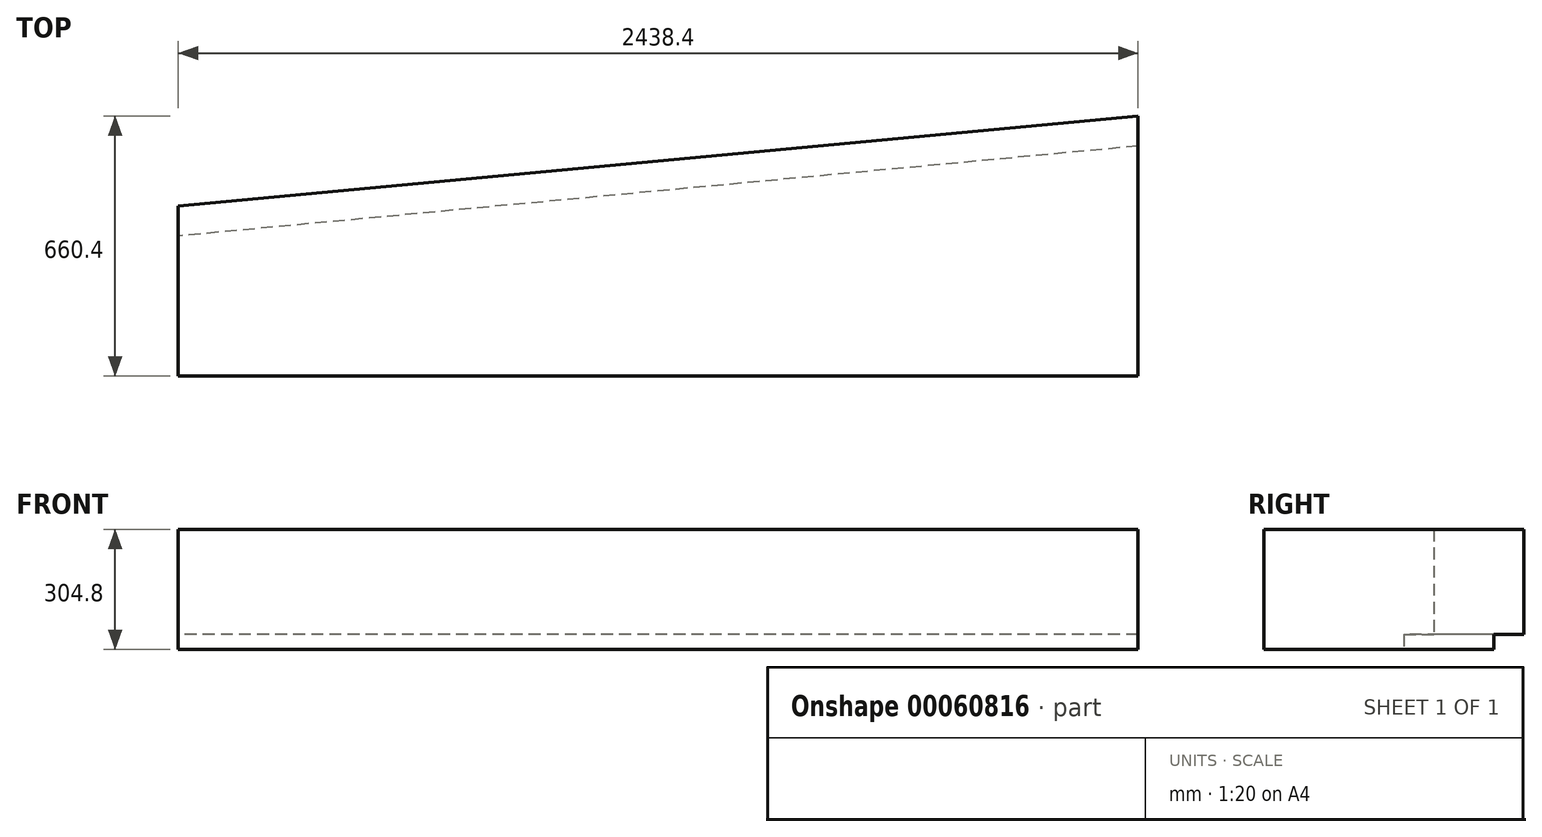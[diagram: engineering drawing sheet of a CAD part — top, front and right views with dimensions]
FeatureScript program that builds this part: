
annotation { "Feature Type Name" : "Feature", "Feature Type Description" : "" }
export const myFeature = defineFeature(function(context is Context, id is Id, definition is map)
    precondition{}
    {
        {
            var Q0;
            Q0=qCreatedBy(makeId("Top.planeOp"),FACE);
            var sketch = newSketch(context, id + "F0", { "sketchPlane" : qUnion([Q0])});
            skLineSegment(sketch, "E0", {"start": v(0, 0) * mm, "end": v(0, 431.8) * mm});
            skLineSegment(sketch, "E1", {"start": v(0, 0) * mm, "end": v(2438.4, 0) * mm});
            skLineSegment(sketch, "E2", {"start": v(2438.4, 0) * mm, "end": v(2438.4, 660.4) * mm});
            skLineSegment(sketch, "E3", {"start": v(2438.4, 660.4) * mm, "end": v(0, 431.8) * mm});
            skSolve(sketch);
        }
        {
            var Q0;
            Q0 = qSketchRegion(id + "F0", true);
            extrude(context, id + "F1", {"entities" : qUnion([Q0]), "depth" : 304.8 * mm});
        }
        {
            var Q0;
            Q0=makeQuery(id+"F1.opExtrude","CAP_FACE",FACE,{"disambiguationData":[OSD([sQuery(id+"F0.wireOp",EDGE,"E0"),sQuery(id+"F0.wireOp",EDGE,"E1"),sQuery(id+"F0.wireOp",EDGE,"E2"),sQuery(id+"F0.wireOp",EDGE,"E3")])],"isStart":true});
            var sketch = newSketch(context, id + "F2", { "sketchPlane" : qUnion([Q0])});
            skLineSegment(sketch, "E4", {"start": v(2438.4, -660.4) * mm, "end": v(2438.4, -584.2) * mm});
            skLineSegment(sketch, "E5", {"start": v(0, -431.8) * mm, "end": v(0, -355.6) * mm});
            skLineSegment(sketch, "E6", {"start": v(2438.4, -584.2) * mm, "end": v(0, -355.6) * mm});
            skLineSegment(sketch, "E7.0", {"start": v(2438.4, -660.4) * mm, "end": v(0, -431.8) * mm});
            skSolve(sketch);
        }
        {
            var Q0;
            Q0 = qSketchRegion(id + "F2", true);
            extrude(context, id + "F3", {"entities" : qUnion([Q0]), "operationType" : NewBodyOperationType.REMOVE, "oppositeDirection" : true, "depth" : 38.1 * mm});
        }
    });
